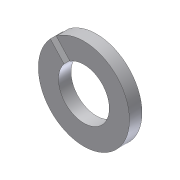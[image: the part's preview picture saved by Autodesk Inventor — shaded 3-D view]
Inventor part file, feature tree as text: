
AUTODESK INVENTOR PART (.ipt)
format: ipt  version: 2012 (Build 160160000, 160)  size: 84,992 bytes
history: native  units: in
note: dims shown in document units (in); Inventor stores cm internally (conversion verified against a paired STEP export)
features: extrude x1, sketch x1
ambient origin geometry x8: Origin, YZ Plane, XZ Plane, XY Plane, X Axis, Y Axis, Z Axis, Center Point
bodies: Solid1 (feature_tree)
feature tree (2):
  extrude  "Extrusion1"  Depth=0.38in
  sketch  "Sketch1"  dims[d0=0.68in d1=0.38in d2=0.06in d3=0.03in d4=0.0938in d5=0.0in]
